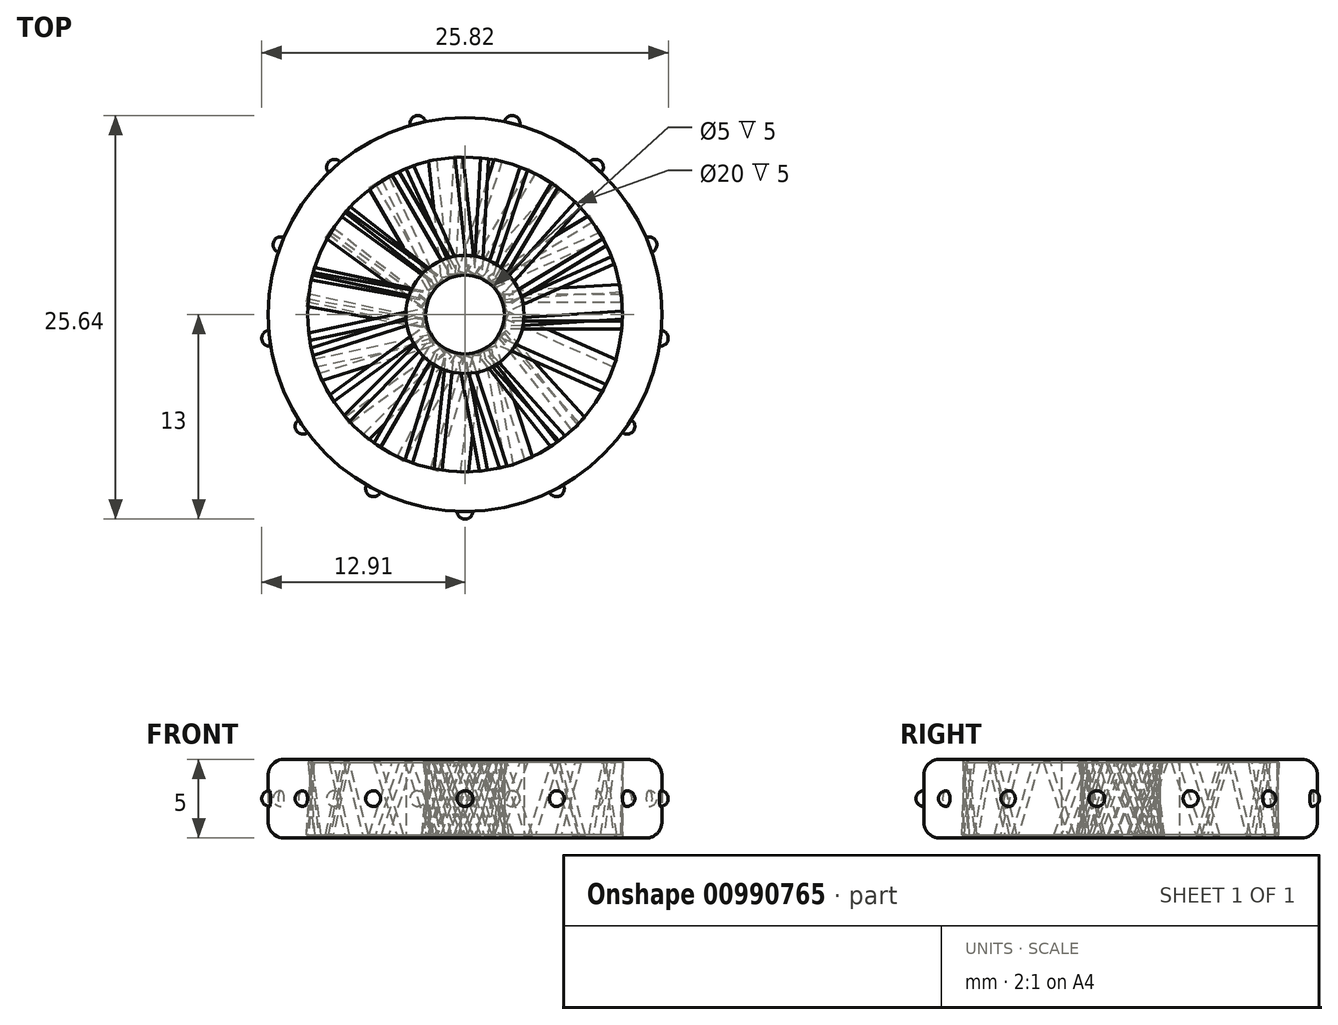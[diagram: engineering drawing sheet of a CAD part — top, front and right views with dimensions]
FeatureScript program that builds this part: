
annotation { "Feature Type Name" : "Feature", "Feature Type Description" : "" }
export const myFeature = defineFeature(function(context is Context, id is Id, definition is map)
    precondition{}
    {
        {
            var Q0;
            Q0=qCreatedBy(makeId("Top.planeOp"),FACE);
            var sketch = newSketch(context, id + "F0", { "sketchPlane" : qUnion([Q0])});
            skCircle(sketch, "E0", {"center": v(0, 0) * mm, "radius": 2.5 * mm});
            skCircle(sketch, "E1", {"center": v(0, 0) * mm, "radius": 3.75 * mm});
            skCircle(sketch, "E2", {"center": v(0, 0) * mm, "radius": 10 * mm});
            skCircle(sketch, "E3", {"center": v(0, 0) * mm, "radius": 12.5 * mm});
            skSolve(sketch);
        }
        {
            var Q0;
            Q0=qCreatedBy(makeId("Right.planeOp"),FACE);
            cPlane(context, id + "F1", {"entities" : qUnion([Q0]), "cplaneType" : CPlaneType.OFFSET, "offset" : 2.5 * mm, "width" : 150 * mm, "height" : 150 * mm});
        }
        {
            var Q0;
            Q0=makeQuery(id+"F0.imprint","IMPRINT",FACE,{"disambiguationData":[TD([[makeQuery(id+"F0.imprint","IMPRINT",EDGE,{"derivedFrom":sQuery(id+"F0.wireOp",EDGE,"E2")}),-1.0]])]});
            var Q1;
            Q1=makeQuery(id+"F0.imprint","IMPRINT",FACE,{"disambiguationData":[TD([[makeQuery(id+"F0.imprint","IMPRINT",EDGE,{"derivedFrom":sQuery(id+"F0.wireOp",EDGE,"E0")}),-1.0]])]});
            extrude(context, id + "F2", {"entities" : qUnion([Q0, Q1]), "endBound" : BoundingType.SYMMETRIC, "depth" : 5 * mm, "offsetDistance" : 25 * mm});
        }
        {
            var Q0;
            Q0=qCreatedBy(id+"F1.planeOp",FACE);
            var sketch = newSketch(context, id + "F3", { "sketchPlane" : qUnion([Q0])});
            skLineSegment(sketch, "E4", {"start": v(-0.93, 2.3) * mm, "end": v(0.78, -2.3) * mm});
            skLineSegment(sketch, "E5", {"start": v(0.78, -2.3) * mm, "end": v(1.28, -2.3) * mm});
            skLineSegment(sketch, "E6", {"start": v(1.28, -2.3) * mm, "end": v(-0.43, 2.3) * mm});
            skLineSegment(sketch, "E7", {"start": v(-0.43, 2.3) * mm, "end": v(-0.93, 2.3) * mm});
            skLineSegment(sketch, "E8", {"start": v(0.42, 0) * mm, "end": v(-0.08, 0) * mm});
            skSolve(sketch);
        }
        {
            var Q0;
            Q0 = qSketchRegion(id + "F3", true);
            extrude(context, id + "F4", {"entities" : qUnion([Q0]), "depth" : 7.5 * mm, "offsetDistance" : 25 * mm});
        }
        {
            var Q0;
            Q0=makeQuery(id+"F4.opExtrude","SWEPT_BODY",BODY,{"disambiguationData":[OSD([sQuery(id+"F3.wireOp",EDGE,"E4"),sQuery(id+"F3.wireOp",EDGE,"E5"),sQuery(id+"F3.wireOp",EDGE,"E6"),sQuery(id+"F3.wireOp",EDGE,"E7")])]});
            var Q1;
            Q1=makeQuery(id+"F2.opExtrude","CAP_EDGE",EDGE,{"disambiguationData":[OSD([sQuery(id+"F0.wireOp",EDGE,"E0")])],"isStart":false});
            circularPattern(context, id + "F5", {"entities" : qUnion([Q0]), "axis" : qUnion([Q1]), "angle" : 360 * degree, "instanceCount" : 15, "equalSpace" : true});
        }
        {
            var Q0;
            Q0=qCreatedBy(makeId("Front.planeOp"),FACE);
            cPlane(context, id + "F6", {"entities" : qUnion([Q0]), "cplaneType" : CPlaneType.OFFSET, "offset" : 12.5 * mm, "width" : 150 * mm, "height" : 150 * mm});
        }
        {
            var Q0;
            Q0=makeQuery(id+"F2.opExtrude","CAP_EDGE",EDGE,{"disambiguationData":[OSD([sQuery(id+"F0.wireOp",EDGE,"E3")])],"isStart":false});
            var Q1;
            Q1=makeQuery(id+"F2.opExtrude","SWEPT_FACE",FACE,{"disambiguationData":[OSD([sQuery(id+"F0.wireOp",EDGE,"E3")])]});
            fillet(context, id + "F7", {"entities" : qUnion([Q0, Q1]), "radius" : 1 * mm, "tangentPropagation" : true, "allowEdgeOverflow" : false});
        }
        {
            var Q0;
            Q0=qCreatedBy(id+"F6.planeOp",FACE);
            var sketch = newSketch(context, id + "F8", { "sketchPlane" : qUnion([Q0])});
            skCircle(sketch, "E9", {"center": v(0, 0) * mm, "radius": 0.5 * mm});
            skSolve(sketch);
        }
        {
            var Q0;
            Q0=makeQuery(id+"F8.imprint","IMPRINT",FACE,{"disambiguationData":[TD([[makeQuery(id+"F8.imprint","IMPRINT",EDGE,{"derivedFrom":sQuery(id+"F8.wireOp",EDGE,"E9")}),1.0]])]});
            extrude(context, id + "F9", {"entities" : qUnion([Q0]), "operationType" : NewBodyOperationType.ADD, "depth" : 0.5 * mm, "offsetDistance" : 25 * mm});
        }
        {
            var Q0;
            Q0=makeQuery(id+"F9.opExtrude","CAP_FACE",FACE,{"disambiguationData":[OSD([sQuery(id+"F8.wireOp",EDGE,"E9")])],"isStart":false});
            fillet(context, id + "F10", {"entities" : qUnion([Q0]), "radius" : 0.5 * mm, "tangentPropagation" : true, "allowEdgeOverflow" : false});
        }
        {
            var Q0;
            Q0=makeQuery(id+"F9.boolean.opBoolean","MERGE",BODY,{"derivedFrom":[makeQuery(id+"F5.opPattern","COPY",BODY,{"derivedFrom":makeQuery(id+"F4.opExtrude","SWEPT_BODY",BODY,{"disambiguationData":[OSD([sQuery(id+"F3.wireOp",EDGE,"E4"),sQuery(id+"F3.wireOp",EDGE,"E5"),sQuery(id+"F3.wireOp",EDGE,"E6"),sQuery(id+"F3.wireOp",EDGE,"E7")])]}),"instanceName":"14"}),makeQuery(id+"F9.opExtrude","SWEPT_BODY",BODY,{"disambiguationData":[OSD([sQuery(id+"F8.wireOp",EDGE,"E9")])]})]});
            var Q1;
            {var subQ0=sQuery(id+"F0.wireOp",EDGE,"E3");Q1=makeQuery(id+"F7.opFillet","BLEND_EDGE",EDGE,{"blendedFrom":[makeQuery(id+"F2.opExtrude","CAP_EDGE",EDGE,{"disambiguationData":[OSD([subQ0])],"isStart":true}),makeQuery(id+"F2.opExtrude","SWEPT_FACE",FACE,{"disambiguationData":[OSD([subQ0])]})],"blendedInto":[makeQuery(id+"F2.opExtrude","SWEPT_FACE",FACE,{"disambiguationData":[OSD([subQ0])]})]});}
            circularPattern(context, id + "F11", {"entities" : qUnion([Q0]), "axis" : qUnion([Q1]), "angle" : 360 * degree, "instanceCount" : 13, "equalSpace" : true});
        }
    });
